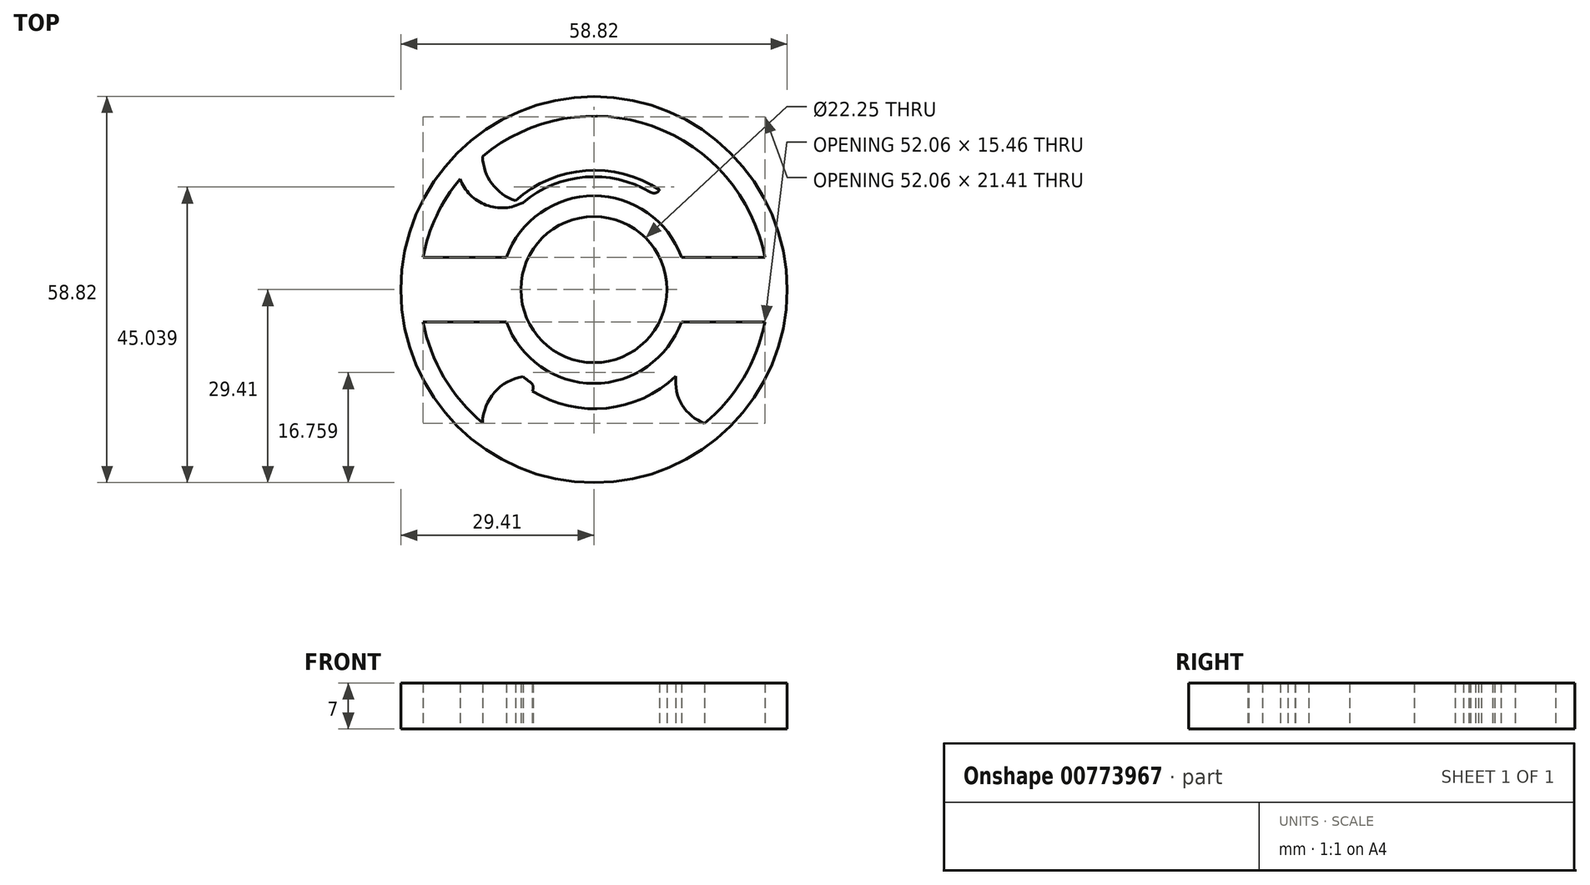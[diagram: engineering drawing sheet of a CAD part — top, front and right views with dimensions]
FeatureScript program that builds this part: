
annotation { "Feature Type Name" : "Feature", "Feature Type Description" : "" }
export const myFeature = defineFeature(function(context is Context, id is Id, definition is map)
    precondition{}
    {
        {
            var Q0;
            Q0=qCreatedBy(makeId("Top.planeOp"),FACE);
            var sketch = newSketch(context, id + "F0", { "sketchPlane" : qUnion([Q0])});
            skCircle(sketch, "E0", {"center": v(0, 0) * mm, "radius": 11.13 * mm});
            skCircle(sketch, "E1", {"center": v(0, 0) * mm, "radius": 29.4 * mm});
            skLineSegment(sketch, "E2", {"start": v(-10.8, 2.7) * mm, "end": v(-29.4, 2.7) * mm});
            skLineSegment(sketch, "E3", {"start": v(-10.83, -2.53) * mm, "end": v(-29.3, -2.53) * mm});
            skLineSegment(sketch, "E4", {"start": v(0, 29.4) * mm, "end": v(0, -29.4) * mm, "construction": true});
            skLineSegment(sketch, "E5", {"start": v(29.4, 0) * mm, "end": v(-29.4, 0) * mm, "construction": true});
            skLineSegment(sketch, "E6.MirrorCS", {"start": v(10.8, 2.7) * mm, "end": v(29.4, 2.7) * mm});
            skLineSegment(sketch, "E7.MirrorCS", {"start": v(10.83, -2.53) * mm, "end": v(29.3, -2.53) * mm});
            skLineSegment(sketch, "E8", {"start": v(-26.03, 4.92) * mm, "end": v(-13.31, 4.92) * mm});
            skLineSegment(sketch, "E9.MirrorCS", {"start": v(26.03, 4.92) * mm, "end": v(13.31, 4.92) * mm});
            skLineSegment(sketch, "E10.MirrorCS", {"start": v(26.03, -4.92) * mm, "end": v(13.31, -4.92) * mm});
            skLineSegment(sketch, "E11.MirrorCS", {"start": v(-26.03, -4.92) * mm, "end": v(-13.31, -4.92) * mm});
            skArc(sketch, "E12", {"start": v(-26.03, -4.92) * mm, "mid": v(0, -26.43) * mm, "end": v(26.03, -4.92) * mm});
            skArc(sketch, "E13", {"start": v(-13.31, -4.92) * mm, "mid": v(0, -14.29) * mm, "end": v(13.31, -4.92) * mm});
            skArc(sketch, "E14.MirrorCS", {"start": v(-26.03, 4.92) * mm, "mid": v(0, 26.43) * mm, "end": v(26.03, 4.92) * mm});
            skArc(sketch, "E15.MirrorCS", {"start": v(-13.31, 4.92) * mm, "mid": v(0, 14.29) * mm, "end": v(13.31, 4.92) * mm});
            skArc(sketch, "E16", {"start": v(5.2, 28.94) * mm, "mid": v(-0.36, 29.38) * mm, "end": v(-5.9, 28.8) * mm});
            skArc(sketch, "E17.1.0", {"start": v(-27.66, -9.98) * mm, "mid": v(-25.26, -15) * mm, "end": v(-22, -19.51) * mm});
            skArc(sketch, "E17.2.0", {"start": v(22.47, -18.97) * mm, "mid": v(25.62, -14.38) * mm, "end": v(27.9, -9.3) * mm});
            skArc(sketch, "E18", {"start": v(-20.38, 16.86) * mm, "mid": v(-16.42, 12.87) * mm, "end": v(-10.81, 13.25) * mm});
            skArc(sketch, "E19", {"start": v(-16.97, 20.28) * mm, "mid": v(-15.15, 15.66) * mm, "end": v(-10.81, 13.25) * mm});
            skArc(sketch, "E20.1.0", {"start": v(-15.32, 21.56) * mm, "mid": v(-12.53, 16.68) * mm, "end": v(-7.01, 15.6) * mm});
            skArc(sketch, "E20.1.1", {"start": v(-11.14, 23.98) * mm, "mid": v(-10.58, 19.05) * mm, "end": v(-7.01, 15.6) * mm});
            skArc(sketch, "E20.2.0", {"start": v(-9.22, 24.8) * mm, "mid": v(-7.79, 19.36) * mm, "end": v(-2.74, 16.88) * mm});
            skArc(sketch, "E20.2.1", {"start": v(-4.55, 26.05) * mm, "mid": v(-5.3, 21.14) * mm, "end": v(-2.74, 16.88) * mm});
            skArc(sketch, "E20.3.0", {"start": v(-2.49, 26.34) * mm, "mid": v(-2.51, 20.71) * mm, "end": v(1.73, 17.02) * mm});
            skArc(sketch, "E20.3.1", {"start": v(2.34, 26.34) * mm, "mid": v(0.36, 21.8) * mm, "end": v(1.73, 17.02) * mm});
            skArc(sketch, "E20.4.0", {"start": v(4.41, 26.08) * mm, "mid": v(2.93, 20.66) * mm, "end": v(6.07, 16) * mm});
            skArc(sketch, "E20.4.1", {"start": v(9.08, 24.84) * mm, "mid": v(5.99, 20.95) * mm, "end": v(6.07, 16) * mm});
            skArc(sketch, "E20.5.0", {"start": v(11.01, 24.05) * mm, "mid": v(8.18, 19.2) * mm, "end": v(10, 13.87) * mm});
            skArc(sketch, "E20.5.1", {"start": v(15.2, 21.64) * mm, "mid": v(11.2, 18.7) * mm, "end": v(10, 13.87) * mm});
            skArc(sketch, "E20.6.0", {"start": v(16.86, 20.38) * mm, "mid": v(12.87, 16.42) * mm, "end": v(13.25, 10.81) * mm});
            skArc(sketch, "E20.6.1", {"start": v(20.28, 16.97) * mm, "mid": v(15.66, 15.15) * mm, "end": v(13.25, 10.81) * mm});
            skLineSegment(sketch, "E20.anchor1", {"start": v(0, 0) * mm, "end": v(-20.38, 16.86) * mm, "construction": true});
            skLineSegment(sketch, "E20.anchor2", {"start": v(0, 0) * mm, "end": v(16.86, 20.38) * mm, "construction": true});
            skArc(sketch, "E21.MirrorCS", {"start": v(20.28, -16.97) * mm, "mid": v(15.66, -15.15) * mm, "end": v(13.25, -10.81) * mm});
            skArc(sketch, "E22.MirrorCS", {"start": v(16.86, -20.38) * mm, "mid": v(12.87, -16.42) * mm, "end": v(13.25, -10.81) * mm});
            skArc(sketch, "E23.MirrorCS", {"start": v(15.2, -21.64) * mm, "mid": v(11.2, -18.7) * mm, "end": v(10, -13.87) * mm});
            skArc(sketch, "E24.MirrorCS", {"start": v(11.01, -24.05) * mm, "mid": v(8.18, -19.2) * mm, "end": v(10, -13.87) * mm});
            skArc(sketch, "E25.MirrorCS", {"start": v(9.08, -24.84) * mm, "mid": v(5.99, -20.95) * mm, "end": v(6.07, -16) * mm});
            skArc(sketch, "E26.MirrorCS", {"start": v(4.41, -26.08) * mm, "mid": v(2.93, -20.66) * mm, "end": v(6.07, -16) * mm});
            skArc(sketch, "E27.MirrorCS", {"start": v(2.34, -26.34) * mm, "mid": v(0.36, -21.8) * mm, "end": v(1.73, -17.02) * mm});
            skArc(sketch, "E28.MirrorCS", {"start": v(-4.55, -26.05) * mm, "mid": v(-5.3, -21.14) * mm, "end": v(-2.74, -16.88) * mm});
            skArc(sketch, "E29.MirrorCS", {"start": v(-2.49, -26.34) * mm, "mid": v(-2.51, -20.71) * mm, "end": v(1.73, -17.02) * mm});
            skArc(sketch, "E30.MirrorCS", {"start": v(-9.22, -24.8) * mm, "mid": v(-7.79, -19.36) * mm, "end": v(-2.74, -16.88) * mm});
            skArc(sketch, "E31.MirrorCS", {"start": v(-11.14, -23.98) * mm, "mid": v(-10.58, -19.05) * mm, "end": v(-7.01, -15.6) * mm});
            skArc(sketch, "E32.MirrorCS", {"start": v(-15.32, -21.56) * mm, "mid": v(-12.53, -16.68) * mm, "end": v(-7.01, -15.6) * mm});
            skArc(sketch, "E33.MirrorCS", {"start": v(-16.97, -20.28) * mm, "mid": v(-15.15, -15.66) * mm, "end": v(-10.81, -13.25) * mm});
            skArc(sketch, "E34.MirrorCS", {"start": v(-20.38, -16.86) * mm, "mid": v(-16.42, -12.87) * mm, "end": v(-10.81, -13.25) * mm});
            skArc(sketch, "E35", {"start": v(-10.81, -13.25) * mm, "mid": v(1.73, -17.1) * mm, "end": v(13.25, -10.81) * mm});
            skArc(sketch, "E36", {"start": v(-11.95, -13.54) * mm, "mid": v(1.12, -18.13) * mm, "end": v(13.57, -12.06) * mm});
            skArc(sketch, "E37.MirrorCS", {"start": v(-11.95, 13.54) * mm, "mid": v(1.12, 18.13) * mm, "end": v(13.57, 12.06) * mm});
            skArc(sketch, "E38.MirrorCS", {"start": v(-10.81, 13.25) * mm, "mid": v(1.73, 17.1) * mm, "end": v(13.25, 10.81) * mm});
            skSolve(sketch);
        }
        {
            var Q0;
            Q0=qSketchRegion(id+"F0",true);
            var Q1;
            {var subQ0=sQuery(id+"F0.wireOp",EDGE,"E18");Q1=makeQuery(id+"F0.imprint","IMPRINT",FACE,{"disambiguationData":[TD([[makeQuery(id+"F0.imprint","IMPRINT",EDGE,{"derivedFrom":subQ0}),1.0]])]});}
            var Q2;
            {var subQ0=sQuery(id+"F0.wireOp",EDGE,"E20.1.0");var subQ1=sQuery(id+"F0.wireOp",EDGE,"E14.MirrorCS");var subQ2=makeQuery(id+"F0.imprint","INTERSECT",VERTEX,{"derivedFrom":[subQ1,subQ0]});Q2=makeQuery(id+"F0.imprint","IMPRINT",FACE,{"disambiguationData":[TD([[makeQuery(id+"F0.imprint","IMPRINT",EDGE,{"disambiguationData":[TD([[subQ2,-1.0]])],"derivedFrom":subQ1}),-1.0]])]});}
            var Q3;
            {var subQ0=sQuery(id+"F0.wireOp",EDGE,"E20.2.0");var subQ1=sQuery(id+"F0.wireOp",EDGE,"E14.MirrorCS");var subQ2=makeQuery(id+"F0.imprint","INTERSECT",VERTEX,{"derivedFrom":[subQ1,subQ0]});Q3=makeQuery(id+"F0.imprint","IMPRINT",FACE,{"disambiguationData":[TD([[makeQuery(id+"F0.imprint","IMPRINT",EDGE,{"disambiguationData":[TD([[subQ2,-1.0]])],"derivedFrom":subQ1}),-1.0]])]});}
            var Q4;
            {var subQ0=sQuery(id+"F0.wireOp",EDGE,"E20.3.0");var subQ1=sQuery(id+"F0.wireOp",EDGE,"E14.MirrorCS");var subQ2=makeQuery(id+"F0.imprint","INTERSECT",VERTEX,{"derivedFrom":[subQ1,subQ0]});Q4=makeQuery(id+"F0.imprint","IMPRINT",FACE,{"disambiguationData":[TD([[makeQuery(id+"F0.imprint","IMPRINT",EDGE,{"disambiguationData":[TD([[subQ2,-1.0]])],"derivedFrom":subQ1}),-1.0]])]});}
            var Q5;
            {var subQ0=sQuery(id+"F0.wireOp",EDGE,"E20.4.0");var subQ1=sQuery(id+"F0.wireOp",EDGE,"E14.MirrorCS");var subQ2=makeQuery(id+"F0.imprint","INTERSECT",VERTEX,{"derivedFrom":[subQ1,subQ0]});Q5=makeQuery(id+"F0.imprint","IMPRINT",FACE,{"disambiguationData":[TD([[makeQuery(id+"F0.imprint","IMPRINT",EDGE,{"disambiguationData":[TD([[subQ2,-1.0]])],"derivedFrom":subQ1}),-1.0]])]});}
            var Q6;
            {var subQ0=sQuery(id+"F0.wireOp",EDGE,"E20.5.0");var subQ1=sQuery(id+"F0.wireOp",EDGE,"E14.MirrorCS");var subQ2=makeQuery(id+"F0.imprint","INTERSECT",VERTEX,{"derivedFrom":[subQ1,subQ0]});Q6=makeQuery(id+"F0.imprint","IMPRINT",FACE,{"disambiguationData":[TD([[makeQuery(id+"F0.imprint","IMPRINT",EDGE,{"disambiguationData":[TD([[subQ2,-1.0]])],"derivedFrom":subQ1}),-1.0]])]});}
            var Q7;
            {var subQ0=sQuery(id+"F0.wireOp",EDGE,"E26.MirrorCS");var subQ1=sQuery(id+"F0.wireOp",EDGE,"E12");var subQ2=makeQuery(id+"F0.imprint","INTERSECT",VERTEX,{"derivedFrom":[subQ1,subQ0]});Q7=makeQuery(id+"F0.imprint","IMPRINT",FACE,{"disambiguationData":[TD([[makeQuery(id+"F0.imprint","IMPRINT",EDGE,{"disambiguationData":[TD([[subQ2,-1.0]])],"derivedFrom":subQ1}),1.0]])]});}
            var Q8;
            {var subQ0=sQuery(id+"F0.wireOp",EDGE,"E29.MirrorCS");var subQ1=sQuery(id+"F0.wireOp",EDGE,"E12");var subQ2=makeQuery(id+"F0.imprint","INTERSECT",VERTEX,{"derivedFrom":[subQ1,subQ0]});Q8=makeQuery(id+"F0.imprint","IMPRINT",FACE,{"disambiguationData":[TD([[makeQuery(id+"F0.imprint","IMPRINT",EDGE,{"disambiguationData":[TD([[subQ2,-1.0]])],"derivedFrom":subQ1}),1.0]])]});}
            var Q9;
            {var subQ0=sQuery(id+"F0.wireOp",EDGE,"E30.MirrorCS");var subQ1=sQuery(id+"F0.wireOp",EDGE,"E12");var subQ2=makeQuery(id+"F0.imprint","INTERSECT",VERTEX,{"derivedFrom":[subQ1,subQ0]});Q9=makeQuery(id+"F0.imprint","IMPRINT",FACE,{"disambiguationData":[TD([[makeQuery(id+"F0.imprint","IMPRINT",EDGE,{"disambiguationData":[TD([[subQ2,-1.0]])],"derivedFrom":subQ1}),1.0]])]});}
            var Q10;
            {var subQ0=sQuery(id+"F0.wireOp",EDGE,"E32.MirrorCS");var subQ1=sQuery(id+"F0.wireOp",EDGE,"E12");var subQ2=makeQuery(id+"F0.imprint","INTERSECT",VERTEX,{"derivedFrom":[subQ1,subQ0]});Q10=makeQuery(id+"F0.imprint","IMPRINT",FACE,{"disambiguationData":[TD([[makeQuery(id+"F0.imprint","IMPRINT",EDGE,{"disambiguationData":[TD([[subQ2,-1.0]])],"derivedFrom":subQ1}),1.0]])]});}
            var Q11;
            {var subQ0=sQuery(id+"F0.wireOp",EDGE,"E33.MirrorCS");Q11=makeQuery(id+"F0.imprint","IMPRINT",FACE,{"disambiguationData":[TD([[makeQuery(id+"F0.imprint","IMPRINT",EDGE,{"derivedFrom":subQ0}),1.0]])]});}
            var Q12;
            {var subQ0=sQuery(id+"F0.wireOp",EDGE,"E24.MirrorCS");var subQ1=sQuery(id+"F0.wireOp",EDGE,"E12");var subQ2=makeQuery(id+"F0.imprint","INTERSECT",VERTEX,{"derivedFrom":[subQ1,subQ0]});Q12=makeQuery(id+"F0.imprint","IMPRINT",FACE,{"disambiguationData":[TD([[makeQuery(id+"F0.imprint","IMPRINT",EDGE,{"disambiguationData":[TD([[subQ2,-1.0]])],"derivedFrom":subQ1}),1.0]])]});}
            var Q13;
            {var subQ0=sQuery(id+"F0.wireOp",EDGE,"E36");var subQ1=sQuery(id+"F0.wireOp",EDGE,"E32.MirrorCS");var subQ2=makeQuery(id+"F0.imprint","INTERSECT",VERTEX,{"derivedFrom":[subQ1,subQ0]});Q13=makeQuery(id+"F0.imprint","IMPRINT",FACE,{"disambiguationData":[TD([[makeQuery(id+"F0.imprint","IMPRINT",EDGE,{"disambiguationData":[TD([[subQ2,-1.0]])],"derivedFrom":subQ1}),1.0]])]});}
            var Q14;
            {var subQ0=sQuery(id+"F0.wireOp",EDGE,"E36");var subQ1=sQuery(id+"F0.wireOp",EDGE,"E30.MirrorCS");var subQ2=makeQuery(id+"F0.imprint","INTERSECT",VERTEX,{"derivedFrom":[subQ1,subQ0]});Q14=makeQuery(id+"F0.imprint","IMPRINT",FACE,{"disambiguationData":[TD([[makeQuery(id+"F0.imprint","IMPRINT",EDGE,{"disambiguationData":[TD([[subQ2,-1.0]])],"derivedFrom":subQ1}),1.0]])]});}
            var Q15;
            {var subQ0=sQuery(id+"F0.wireOp",EDGE,"E36");var subQ1=sQuery(id+"F0.wireOp",EDGE,"E28.MirrorCS");var subQ2=makeQuery(id+"F0.imprint","INTERSECT",VERTEX,{"derivedFrom":[subQ1,subQ0]});Q15=makeQuery(id+"F0.imprint","IMPRINT",FACE,{"disambiguationData":[TD([[makeQuery(id+"F0.imprint","IMPRINT",EDGE,{"disambiguationData":[TD([[subQ2,-1.0]])],"derivedFrom":subQ1}),-1.0]])]});}
            var Q16;
            {var subQ0=sQuery(id+"F0.wireOp",EDGE,"E36");var subQ1=sQuery(id+"F0.wireOp",EDGE,"E26.MirrorCS");var subQ2=makeQuery(id+"F0.imprint","INTERSECT",VERTEX,{"derivedFrom":[subQ1,subQ0]});Q16=makeQuery(id+"F0.imprint","IMPRINT",FACE,{"disambiguationData":[TD([[makeQuery(id+"F0.imprint","IMPRINT",EDGE,{"disambiguationData":[TD([[subQ2,-1.0]])],"derivedFrom":subQ1}),1.0]])]});}
            var Q17;
            {var subQ0=sQuery(id+"F0.wireOp",EDGE,"E36");var subQ1=sQuery(id+"F0.wireOp",EDGE,"E24.MirrorCS");var subQ2=makeQuery(id+"F0.imprint","INTERSECT",VERTEX,{"derivedFrom":[subQ1,subQ0]});Q17=makeQuery(id+"F0.imprint","IMPRINT",FACE,{"disambiguationData":[TD([[makeQuery(id+"F0.imprint","IMPRINT",EDGE,{"disambiguationData":[TD([[subQ2,-1.0]])],"derivedFrom":subQ1}),1.0]])]});}
            var Q18;
            {var subQ0=sQuery(id+"F0.wireOp",EDGE,"E36");var subQ1=sQuery(id+"F0.wireOp",EDGE,"E23.MirrorCS");var subQ2=makeQuery(id+"F0.imprint","INTERSECT",VERTEX,{"derivedFrom":[subQ1,subQ0]});Q18=makeQuery(id+"F0.imprint","IMPRINT",FACE,{"disambiguationData":[TD([[makeQuery(id+"F0.imprint","IMPRINT",EDGE,{"disambiguationData":[TD([[subQ2,-1.0]])],"derivedFrom":subQ1}),1.0]])]});}
            var Q19;
            {var subQ0=sQuery(id+"F0.wireOp",EDGE,"E36");var subQ1=sQuery(id+"F0.wireOp",EDGE,"E25.MirrorCS");var subQ2=makeQuery(id+"F0.imprint","INTERSECT",VERTEX,{"derivedFrom":[subQ1,subQ0]});Q19=makeQuery(id+"F0.imprint","IMPRINT",FACE,{"disambiguationData":[TD([[makeQuery(id+"F0.imprint","IMPRINT",EDGE,{"disambiguationData":[TD([[subQ2,-1.0]])],"derivedFrom":subQ1}),1.0]])]});}
            var Q20;
            {var subQ0=sQuery(id+"F0.wireOp",EDGE,"E36");var subQ1=sQuery(id+"F0.wireOp",EDGE,"E27.MirrorCS");var subQ2=makeQuery(id+"F0.imprint","INTERSECT",VERTEX,{"derivedFrom":[subQ1,subQ0]});Q20=makeQuery(id+"F0.imprint","IMPRINT",FACE,{"disambiguationData":[TD([[makeQuery(id+"F0.imprint","IMPRINT",EDGE,{"disambiguationData":[TD([[subQ2,-1.0]])],"derivedFrom":subQ1}),1.0]])]});}
            var Q21;
            {var subQ0=sQuery(id+"F0.wireOp",EDGE,"E36");var subQ1=sQuery(id+"F0.wireOp",EDGE,"E28.MirrorCS");var subQ2=makeQuery(id+"F0.imprint","INTERSECT",VERTEX,{"derivedFrom":[subQ1,subQ0]});Q21=makeQuery(id+"F0.imprint","IMPRINT",FACE,{"disambiguationData":[TD([[makeQuery(id+"F0.imprint","IMPRINT",EDGE,{"disambiguationData":[TD([[subQ2,-1.0]])],"derivedFrom":subQ1}),1.0]])]});}
            var Q22;
            {var subQ0=sQuery(id+"F0.wireOp",EDGE,"E36");var subQ1=sQuery(id+"F0.wireOp",EDGE,"E31.MirrorCS");var subQ2=makeQuery(id+"F0.imprint","INTERSECT",VERTEX,{"derivedFrom":[subQ1,subQ0]});Q22=makeQuery(id+"F0.imprint","IMPRINT",FACE,{"disambiguationData":[TD([[makeQuery(id+"F0.imprint","IMPRINT",EDGE,{"disambiguationData":[TD([[subQ2,-1.0]])],"derivedFrom":subQ1}),1.0]])]});}
            var Q23;
            {var subQ3=sQuery(id+"F0.wireOp",EDGE,"E37.MirrorCS");var subQ5=sQuery(id+"F0.wireOp",EDGE,"E20.1.0");var subQ7=makeQuery(id+"F0.imprint","INTERSECT",VERTEX,{"derivedFrom":[subQ5,subQ3]});Q23=makeQuery(id+"F0.imprint","IMPRINT",FACE,{"disambiguationData":[TD([[makeQuery(id+"F0.imprint","IMPRINT",EDGE,{"disambiguationData":[TD([[subQ7,-1.0]])],"derivedFrom":subQ5}),-1.0]])]});}
            var Q24;
            {var subQ0=sQuery(id+"F0.wireOp",EDGE,"E37.MirrorCS");var subQ1=sQuery(id+"F0.wireOp",EDGE,"E20.2.0");var subQ2=makeQuery(id+"F0.imprint","INTERSECT",VERTEX,{"derivedFrom":[subQ1,subQ0]});Q24=makeQuery(id+"F0.imprint","IMPRINT",FACE,{"disambiguationData":[TD([[makeQuery(id+"F0.imprint","IMPRINT",EDGE,{"disambiguationData":[TD([[subQ2,-1.0]])],"derivedFrom":subQ1}),1.0]])]});}
            var Q25;
            {var subQ0=sQuery(id+"F0.wireOp",EDGE,"E37.MirrorCS");var subQ1=sQuery(id+"F0.wireOp",EDGE,"E20.3.1");var subQ2=makeQuery(id+"F0.imprint","INTERSECT",VERTEX,{"derivedFrom":[subQ1,subQ0]});Q25=makeQuery(id+"F0.imprint","IMPRINT",FACE,{"disambiguationData":[TD([[makeQuery(id+"F0.imprint","IMPRINT",EDGE,{"disambiguationData":[TD([[subQ2,-1.0]])],"derivedFrom":subQ1}),1.0]])]});}
            var Q26;
            {var subQ0=sQuery(id+"F0.wireOp",EDGE,"E37.MirrorCS");var subQ1=sQuery(id+"F0.wireOp",EDGE,"E20.1.0");var subQ2=makeQuery(id+"F0.imprint","INTERSECT",VERTEX,{"derivedFrom":[subQ1,subQ0]});Q26=makeQuery(id+"F0.imprint","IMPRINT",FACE,{"disambiguationData":[TD([[makeQuery(id+"F0.imprint","IMPRINT",EDGE,{"disambiguationData":[TD([[subQ2,-1.0]])],"derivedFrom":subQ1}),1.0]])]});}
            var Q27;
            {var subQ0=sQuery(id+"F0.wireOp",EDGE,"E37.MirrorCS");var subQ1=sQuery(id+"F0.wireOp",EDGE,"E20.1.1");var subQ2=makeQuery(id+"F0.imprint","INTERSECT",VERTEX,{"derivedFrom":[subQ1,subQ0]});Q27=makeQuery(id+"F0.imprint","IMPRINT",FACE,{"disambiguationData":[TD([[makeQuery(id+"F0.imprint","IMPRINT",EDGE,{"disambiguationData":[TD([[subQ2,-1.0]])],"derivedFrom":subQ1}),1.0]])]});}
            var Q28;
            {var subQ0=sQuery(id+"F0.wireOp",EDGE,"E37.MirrorCS");var subQ1=sQuery(id+"F0.wireOp",EDGE,"E20.2.1");var subQ2=makeQuery(id+"F0.imprint","INTERSECT",VERTEX,{"derivedFrom":[subQ1,subQ0]});Q28=makeQuery(id+"F0.imprint","IMPRINT",FACE,{"disambiguationData":[TD([[makeQuery(id+"F0.imprint","IMPRINT",EDGE,{"disambiguationData":[TD([[subQ2,-1.0]])],"derivedFrom":subQ1}),1.0]])]});}
            var Q29;
            {var subQ0=sQuery(id+"F0.wireOp",EDGE,"E37.MirrorCS");var subQ1=sQuery(id+"F0.wireOp",EDGE,"E20.4.0");var subQ2=makeQuery(id+"F0.imprint","INTERSECT",VERTEX,{"derivedFrom":[subQ1,subQ0]});Q29=makeQuery(id+"F0.imprint","IMPRINT",FACE,{"disambiguationData":[TD([[makeQuery(id+"F0.imprint","IMPRINT",EDGE,{"disambiguationData":[TD([[subQ2,-1.0]])],"derivedFrom":subQ1}),1.0]])]});}
            var Q30;
            {var subQ0=sQuery(id+"F0.wireOp",EDGE,"E37.MirrorCS");var subQ1=sQuery(id+"F0.wireOp",EDGE,"E20.4.1");var subQ2=makeQuery(id+"F0.imprint","INTERSECT",VERTEX,{"derivedFrom":[subQ1,subQ0]});Q30=makeQuery(id+"F0.imprint","IMPRINT",FACE,{"disambiguationData":[TD([[makeQuery(id+"F0.imprint","IMPRINT",EDGE,{"disambiguationData":[TD([[subQ2,-1.0]])],"derivedFrom":subQ1}),1.0]])]});}
            var Q31;
            {var subQ0=sQuery(id+"F0.wireOp",EDGE,"E37.MirrorCS");var subQ1=sQuery(id+"F0.wireOp",EDGE,"E20.3.0");var subQ2=makeQuery(id+"F0.imprint","INTERSECT",VERTEX,{"derivedFrom":[subQ1,subQ0]});Q31=makeQuery(id+"F0.imprint","IMPRINT",FACE,{"disambiguationData":[TD([[makeQuery(id+"F0.imprint","IMPRINT",EDGE,{"disambiguationData":[TD([[subQ2,-1.0]])],"derivedFrom":subQ1}),1.0]])]});}
            var Q32;
            {var subQ0=sQuery(id+"F0.wireOp",EDGE,"E37.MirrorCS");var subQ1=sQuery(id+"F0.wireOp",EDGE,"E20.5.0");var subQ2=makeQuery(id+"F0.imprint","INTERSECT",VERTEX,{"derivedFrom":[subQ1,subQ0]});Q32=makeQuery(id+"F0.imprint","IMPRINT",FACE,{"disambiguationData":[TD([[makeQuery(id+"F0.imprint","IMPRINT",EDGE,{"disambiguationData":[TD([[subQ2,-1.0]])],"derivedFrom":subQ1}),1.0]])]});}
            extrude(context, id + "F1", {"entities" : qUnion([Q0, Q1, Q2, Q3, Q4, Q5, Q6, Q7, Q8, Q9, Q10, Q11, Q12, Q13, Q14, Q15, Q16, Q17, Q18, Q19, Q20, Q21, Q22, Q23, Q24, Q25, Q26, Q27, Q28, Q29, Q30, Q31, Q32]), "depth" : 7 * mm, "offsetDistance" : 25 * mm});
        }
        {
            var Q0;
            Q0=makeQuery(id+"F1.opExtrude","SWEPT_EDGE",EDGE,{"disambiguationData":[OSD([sQuery(id+"F0.wireOp",EDGE,"E20.5.1"),sQuery(id+"F0.wireOp",EDGE,"E38.MirrorCS")])]});
            var Q1;
            Q1=makeQuery(id+"F1.opExtrude","SWEPT_EDGE",EDGE,{"disambiguationData":[OSD([sQuery(id+"F0.wireOp",EDGE,"E23.MirrorCS"),sQuery(id+"F0.wireOp",EDGE,"E35")])]});
            fillet(context, id + "F2", {"entities" : qUnion([Q0, Q1]), "radius" : 0.98 * mm, "tangentPropagation" : true, "allowEdgeOverflow" : false});
        }
    });
